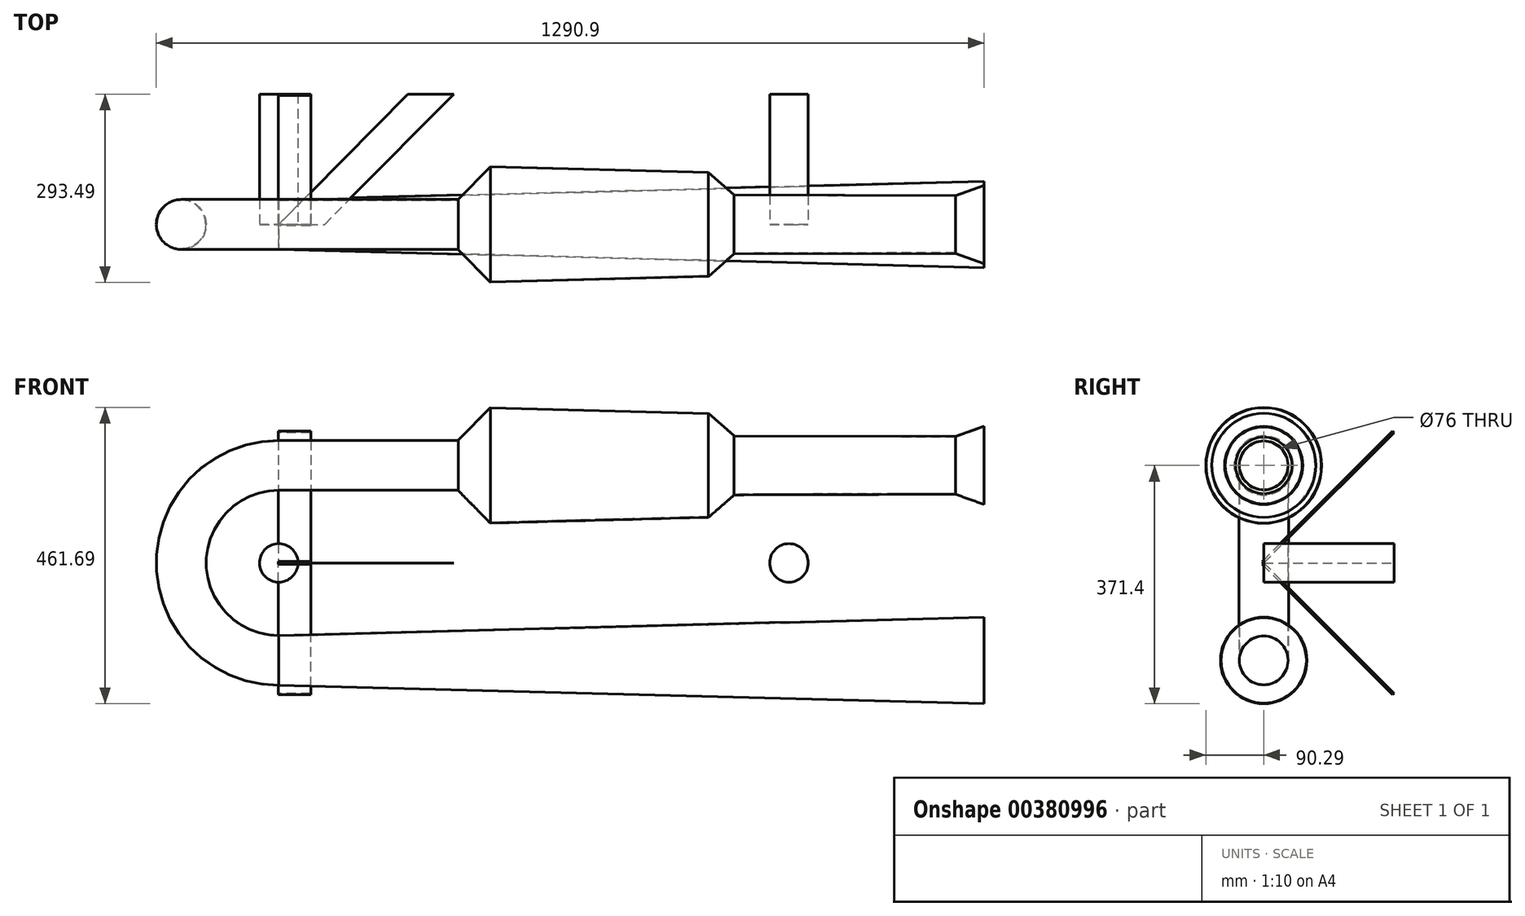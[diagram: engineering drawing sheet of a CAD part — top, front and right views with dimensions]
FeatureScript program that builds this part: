
annotation { "Feature Type Name" : "Feature", "Feature Type Description" : "" }
export const myFeature = defineFeature(function(context is Context, id is Id, definition is map)
    precondition{}
    {
        {
            var Q0;
            Q0=qCreatedBy(makeId("Front.planeOp"),FACE);
            var sketch = newSketch(context, id + "F0", { "sketchPlane" : qUnion([Q0])});
            skLineSegment(sketch, "E0", {"start": v(0, -60) * mm, "end": v(-45, -44) * mm});
            skLineSegment(sketch, "E1", {"start": v(-45, -44) * mm, "end": v(-45, -44.96) * mm});
            skLineSegment(sketch, "E2", {"start": v(-45, -44.96) * mm, "end": v(-0.3, -60.85) * mm});
            skLineSegment(sketch, "E3", {"start": v(-0.3, -60.85) * mm, "end": v(0, -60) * mm});
            skLineSegment(sketch, "E4", {"start": v(0, 0) * mm, "end": v(-1100, 0) * mm, "construction": true});
            skLineSegment(sketch, "E5", {"start": v(-45, -44) * mm, "end": v(-390, -45) * mm});
            skLineSegment(sketch, "E6", {"start": v(-45, -44.96) * mm, "end": v(-390, -45.96) * mm});
            skLineSegment(sketch, "E7", {"start": v(-390, -45.96) * mm, "end": v(-390, -45) * mm});
            skLineSegment(sketch, "E8", {"start": v(-390, -45) * mm, "end": v(-430, -80) * mm});
            skLineSegment(sketch, "E9", {"start": v(-390, -46.2) * mm, "end": v(-430, -81.2) * mm});
            skLineSegment(sketch, "E10", {"start": v(-390, -45.96) * mm, "end": v(-390, -46.2) * mm});
            skLineSegment(sketch, "E11", {"start": v(-430, -80) * mm, "end": v(-430, -81.2) * mm});
            skLineSegment(sketch, "E12", {"start": v(-430, -80) * mm, "end": v(-770, -89) * mm});
            skLineSegment(sketch, "E13", {"start": v(-430, -80.9) * mm, "end": v(-770, -89.9) * mm});
            skLineSegment(sketch, "E14", {"start": v(-770, -89) * mm, "end": v(-770, -89.9) * mm});
            skLineSegment(sketch, "E15", {"start": v(-770, -89) * mm, "end": v(-820, -38) * mm});
            skLineSegment(sketch, "E16", {"start": v(-770, -90.29) * mm, "end": v(-820, -39.29) * mm});
            skLineSegment(sketch, "E17", {"start": v(-770, -89.9) * mm, "end": v(-770, -90.29) * mm});
            skLineSegment(sketch, "E18", {"start": v(-820, -38) * mm, "end": v(-820, -39.29) * mm});
            skLineSegment(sketch, "E19", {"start": v(-820, -38) * mm, "end": v(-1100, -38) * mm});
            skLineSegment(sketch, "E20", {"start": v(-820, -38.9) * mm, "end": v(-1100, -38.9) * mm});
            skLineSegment(sketch, "E21", {"start": v(-1100, -38) * mm, "end": v(-1100, -38.9) * mm});
            skLineSegment(sketch, "E22", {"start": v(-1100, -38) * mm, "end": v(-1100, 0) * mm, "construction": true});
            skLineSegment(sketch, "E23", {"start": v(-1100, 0) * mm, "end": v(-1100, -152) * mm, "construction": true});
            skArc(sketch, "E24", {"start": v(-1100, -38) * mm, "mid": v(-1214, -152) * mm, "end": v(-1100, -266) * mm});
            skArc(sketch, "E25", {"start": v(-1100, 0) * mm, "mid": v(-1252, -152) * mm, "end": v(-1100, -304) * mm, "construction": true});
            skArc(sketch, "E26", {"start": v(-1100, -38.9) * mm, "mid": v(-1213.1, -152) * mm, "end": v(-1100, -265.1) * mm});
            skLineSegment(sketch, "E27", {"start": v(-1100, -265.1) * mm, "end": v(-1100, -266) * mm});
            skLineSegment(sketch, "E28", {"start": v(-1100, -304) * mm, "end": v(332.26, -304) * mm, "construction": true});
            skLineSegment(sketch, "E29", {"start": v(-1100, -266) * mm, "end": v(0, -237.5) * mm});
            skLineSegment(sketch, "E30", {"start": v(-1100, -265.1) * mm, "end": v(0, -236.6) * mm});
            skLineSegment(sketch, "E31", {"start": v(0, -236.6) * mm, "end": v(0, -237.5) * mm});
            skCircle(sketch, "E32", {"center": v(-1100, -152) * mm, "radius": 30 * mm});
            skCircle(sketch, "E33", {"center": v(-304.43, -152) * mm, "radius": 30 * mm});
            skSolve(sketch);
        }
        {
            var Q0;
            Q0=makeQuery(id+"F0.imprint","IMPRINT",FACE,{"disambiguationData":[TD([[makeQuery(id+"F0.imprint","IMPRINT",EDGE,{"derivedFrom":sQuery(id+"F0.wireOp",EDGE,"E0")}),1.0]])]});
            var Q1;
            Q1=makeQuery(id+"F0.imprint","IMPRINT",FACE,{"disambiguationData":[TD([[makeQuery(id+"F0.imprint","IMPRINT",EDGE,{"derivedFrom":sQuery(id+"F0.wireOp",EDGE,"E1")}),-1.0]])]});
            var Q2;
            Q2=makeQuery(id+"F0.imprint","IMPRINT",FACE,{"disambiguationData":[TD([[makeQuery(id+"F0.imprint","IMPRINT",EDGE,{"derivedFrom":sQuery(id+"F0.wireOp",EDGE,"E7")}),1.0]])]});
            var Q3;
            {var subQ0=sQuery(id+"F0.wireOp",EDGE,"E12");Q3=makeQuery(id+"F0.imprint","IMPRINT",FACE,{"disambiguationData":[TD([[makeQuery(id+"F0.imprint","IMPRINT",EDGE,{"derivedFrom":subQ0}),1.0]])]});}
            var Q4;
            Q4=makeQuery(id+"F0.imprint","IMPRINT",FACE,{"disambiguationData":[TD([[makeQuery(id+"F0.imprint","IMPRINT",EDGE,{"derivedFrom":sQuery(id+"F0.wireOp",EDGE,"E14")}),-1.0]])]});
            var Q5;
            {var subQ0=sQuery(id+"F0.wireOp",EDGE,"E19");Q5=makeQuery(id+"F0.imprint","IMPRINT",FACE,{"disambiguationData":[TD([[makeQuery(id+"F0.imprint","IMPRINT",EDGE,{"derivedFrom":subQ0}),1.0]])]});}
            var Q6;
            Q6=sQuery(id+"F0.wireOp",EDGE,"E4");
            revolve(context, id + "F1", {"entities" : qUnion([Q0, Q1, Q2, Q3, Q4, Q5]), "axis" : qUnion([Q6]), "revolveType" : RevolveType.FULL});
        }
        {
            var Q0;
            Q0=makeQuery(id+"F1.opRevolve","SWEPT_FACE",FACE,{"disambiguationData":[OSD([sQuery(id+"F0.wireOp",EDGE,"E21")])]});
            var Q1;
            Q1=sQuery(id+"F0.wireOp",EDGE,"E26");
            sweep(context, id + "F2", {"operationType" : NewBodyOperationType.ADD, "profiles" : qUnion([Q0]), "path" : qUnion([Q1])});
        }
        {
            var Q0;
            {var subQ3=sQuery(id+"F0.wireOp",EDGE,"E29");Q0=makeQuery(id+"F0.imprint","IMPRINT",FACE,{"disambiguationData":[TD([[makeQuery(id+"F0.imprint","IMPRINT",EDGE,{"derivedFrom":subQ3}),1.0]])]});}
            var Q1;
            Q1=sQuery(id+"F0.wireOp",EDGE,"E28");
            revolve(context, id + "F3", {"operationType" : NewBodyOperationType.ADD, "entities" : qUnion([Q0]), "axis" : qUnion([Q1]), "revolveType" : RevolveType.FULL});
        }
        {
            var Q0;
            Q0=makeQuery(id+"F0.imprint","IMPRINT",FACE,{"disambiguationData":[TD([[makeQuery(id+"F0.imprint","IMPRINT",EDGE,{"derivedFrom":sQuery(id+"F0.wireOp",EDGE,"E32")}),1.0]])]});
            var Q1;
            Q1=makeQuery(id+"F0.imprint","IMPRINT",FACE,{"disambiguationData":[TD([[makeQuery(id+"F0.imprint","IMPRINT",EDGE,{"derivedFrom":sQuery(id+"F0.wireOp",EDGE,"E33")}),1.0]])]});
            extrude(context, id + "F4", {"entities" : qUnion([Q0, Q1]), "oppositeDirection" : true, "depth" : 203.2 * mm, "offsetDistance" : 25 * mm});
        }
        {
            var Q0;
            Q0=qCreatedBy(makeId("Right.planeOp"),FACE);
            cPlane(context, id + "F5", {"entities" : qUnion([Q0]), "cplaneType" : CPlaneType.OFFSET, "offset" : 1101 * mm, "oppositeDirection" : true, "width" : 150 * mm, "height" : 150 * mm});
        }
        {
            var Q0;
            Q0=qCreatedBy(id+"F5.planeOp",FACE);
            var sketch = newSketch(context, id + "F6", { "sketchPlane" : qUnion([Q0])});
            skLineSegment(sketch, "E34", {"start": v(0, -152) * mm, "end": v(203.2, 51.2) * mm});
            skLineSegment(sketch, "E35", {"start": v(203.2, 51.2) * mm, "end": v(200.95, 53.45) * mm});
            skLineSegment(sketch, "E36", {"start": v(200.95, 53.45) * mm, "end": v(-2.25, -149.75) * mm});
            skLineSegment(sketch, "E37", {"start": v(-2.25, -149.75) * mm, "end": v(0, -152) * mm});
            skLineSegment(sketch, "E38", {"start": v(0, -152) * mm, "end": v(203.2, -355.2) * mm});
            skLineSegment(sketch, "E39", {"start": v(203.2, -355.2) * mm, "end": v(200.95, -357.45) * mm});
            skLineSegment(sketch, "E40", {"start": v(200.95, -357.45) * mm, "end": v(-2.25, -154.25) * mm});
            skLineSegment(sketch, "E41", {"start": v(-2.25, -154.25) * mm, "end": v(0, -152) * mm});
            skSolve(sketch);
        }
        {
            var Q0;
            Q0=makeQuery(id+"F6.imprint","IMPRINT",FACE,{"disambiguationData":[TD([[makeQuery(id+"F6.imprint","IMPRINT",EDGE,{"derivedFrom":sQuery(id+"F6.wireOp",EDGE,"E34")}),1.0]])]});
            var Q1;
            Q1=makeQuery(id+"F6.imprint","IMPRINT",FACE,{"disambiguationData":[TD([[makeQuery(id+"F6.imprint","IMPRINT",EDGE,{"derivedFrom":sQuery(id+"F6.wireOp",EDGE,"E38")}),-1.0]])]});
            extrude(context, id + "F7", {"entities" : qUnion([Q0, Q1]), "depth" : 50.8 * mm, "offsetDistance" : 25 * mm});
        }
        {
            var Q0;
            Q0=qCreatedBy(makeId("Top.planeOp"),FACE);
            cPlane(context, id + "F8", {"entities" : qUnion([Q0]), "cplaneType" : CPlaneType.OFFSET, "offset" : 152 * mm, "oppositeDirection" : true, "width" : 150 * mm, "height" : 150 * mm});
        }
        {
            var Q0;
            Q0=qCreatedBy(id+"F8.planeOp",FACE);
            var sketch = newSketch(context, id + "F9", { "sketchPlane" : qUnion([Q0])});
            skLineSegment(sketch, "E42", {"start": v(-1028.49, 0) * mm, "end": v(-827.16, 203.2) * mm});
            skLineSegment(sketch, "E43", {"start": v(-898.67, 203.2) * mm, "end": v(-1100, 0) * mm});
            skLineSegment(sketch, "E44", {"start": v(-827.16, 203.2) * mm, "end": v(-898.67, 203.2) * mm});
            skLineSegment(sketch, "E45", {"start": v(-1100, 0) * mm, "end": v(-1028.49, 0) * mm});
            skSolve(sketch);
        }
        {
            var Q0;
            Q0=makeQuery(id+"F9.imprint","IMPRINT",FACE,{"disambiguationData":[TD([[makeQuery(id+"F9.imprint","IMPRINT",EDGE,{"derivedFrom":sQuery(id+"F9.wireOp",EDGE,"E42")}),1.0]])]});
            extrude(context, id + "F10", {"entities" : qUnion([Q0]), "endBound" : BoundingType.SYMMETRIC, "oppositeDirection" : true, "depth" : 1 / 203.2 * mm, "offsetDistance" : 25 * mm});
        }
    });
